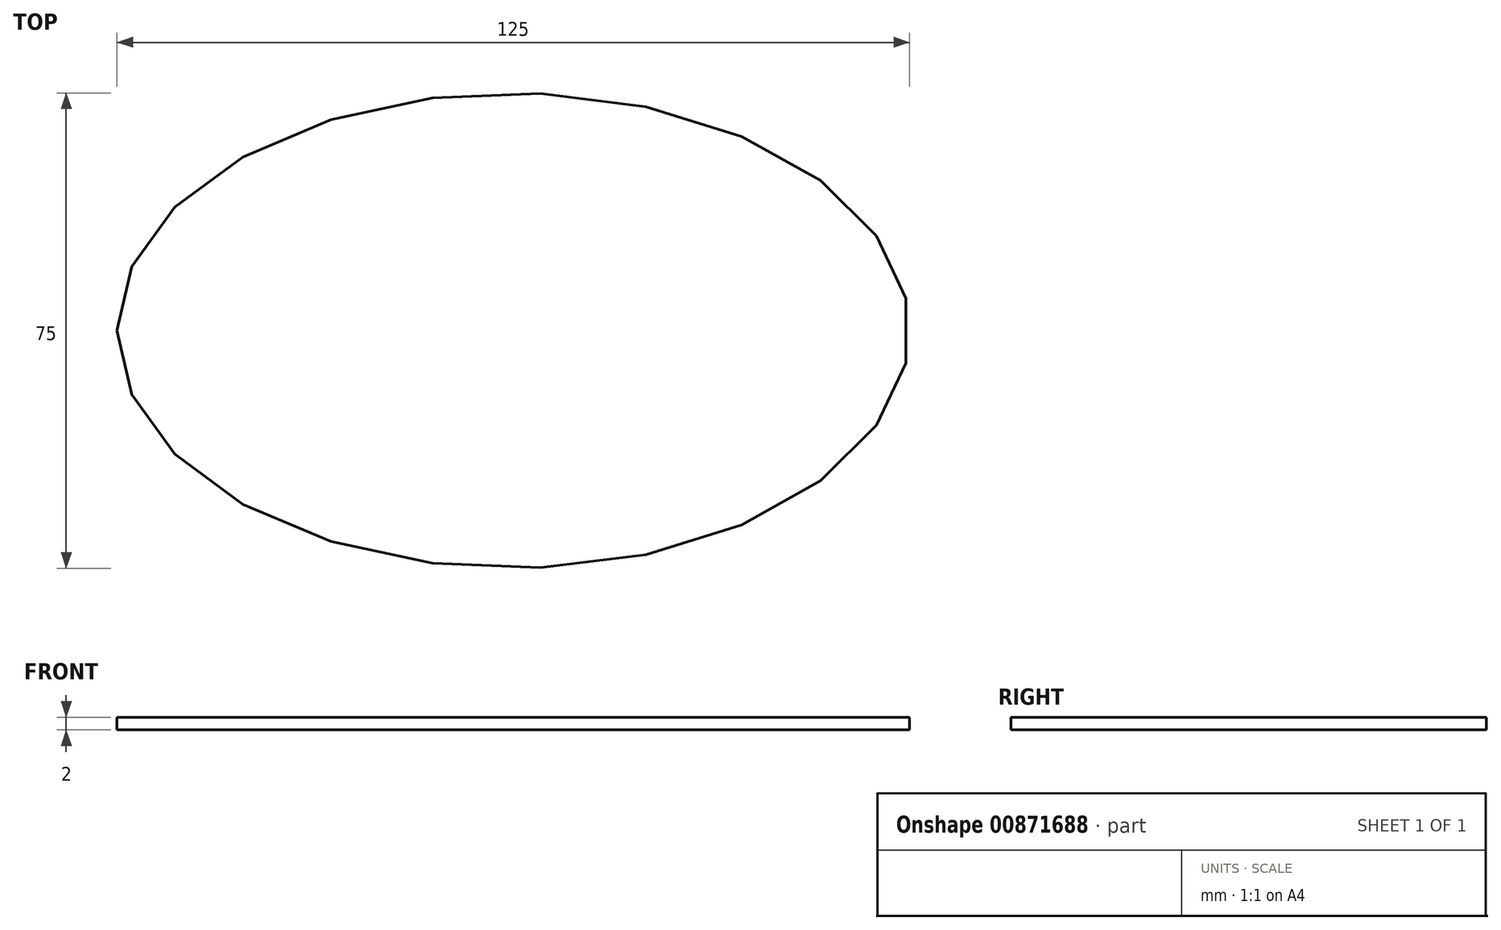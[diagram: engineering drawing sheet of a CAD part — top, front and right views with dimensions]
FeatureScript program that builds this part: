
annotation { "Feature Type Name" : "Feature", "Feature Type Description" : "" }
export const myFeature = defineFeature(function(context is Context, id is Id, definition is map)
    precondition{}
    {
        {
            var Q0;
            Q0=qCreatedBy(makeId("Top.planeOp"),FACE);
            var sketch = newSketch(context, id + "F0", { "sketchPlane" : qUnion([Q0])});
            skEllipse(sketch, "E0", {"center": v(0, 0) * mm, "majorRadius": 62.5 * mm, "minorRadius": 37.5 * mm, "majorAxis": v(-1, 0)});
            skSolve(sketch);
        }
        {
            var Q0;
            Q0=makeQuery(id+"F0.imprint","IMPRINT",FACE,{"disambiguationData":[TD([[makeQuery(id+"F0.imprint","IMPRINT",EDGE,{"derivedFrom":sQuery(id+"F0.wireOp",EDGE,"E0")}),1.0]])]});
            extrude(context, id + "F1", {"entities" : qUnion([Q0]), "depth" : 2 * mm, "offsetDistance" : 25 * mm});
        }
    });
